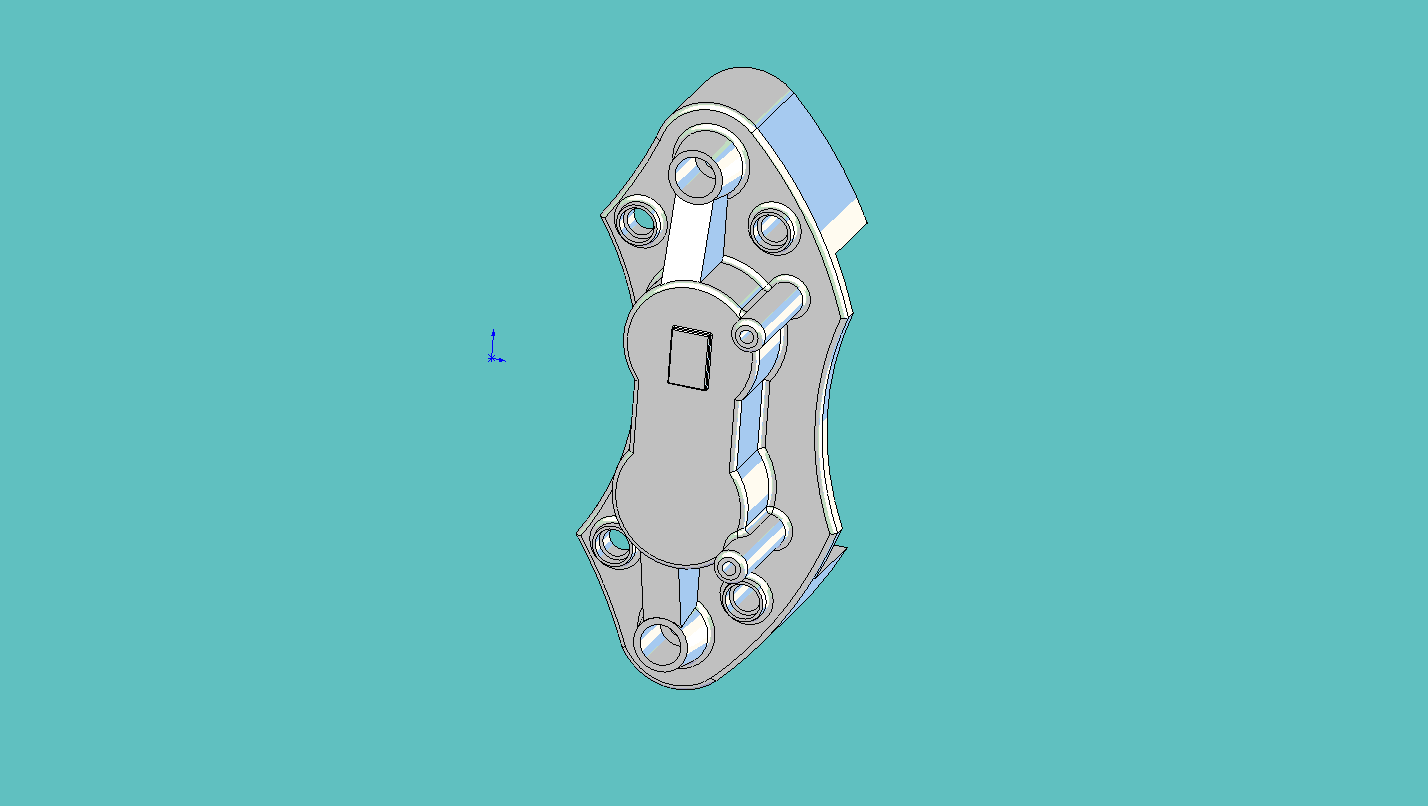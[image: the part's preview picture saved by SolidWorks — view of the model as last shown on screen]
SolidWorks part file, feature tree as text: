
SOLIDWORKS PART (.sldprt)
format: sldprt  version: not decoded by parser v0  size: 2,216,448 bytes
history: native  units: mm
features: sketch x25, cut_extrude x14, fillet x9, extrude x7, mirror x4, plane x3, material x1, chamfer x1, delete_body x1 (+14 scaffold rows collapsed)
feature tree (79):
  scaffold x14  (default folders/planes/origin — collapsed)
  material  "Material <not specified>"
  sketch  "Sketch1"  dims[D1=63.5mm]
  extrude  "Extrude1"  Depth=31.75mm
  sketch  "Sketch5"  dims[D1=~43.962388mm]
  extrude  "Extrude2"  Depth=50.8mm
  sketch  "Sketch3"  dims[D1=50.0mm]
  cut_extrude  "Cut-Extrude1"  Depth=25.4mm
  sketch  "Sketch7"  dims[c1.D1=12.7mm c1.D2=12.7mm c2.D1=~13.906952mm c2.D2=25.0mm c2.D3=25.0mm c3.D1=~12.799272mm c3.D3=152.4mm]
  fillet  "Fillet1"  Radius=2.54mm
  fillet  "Fillet2"  Radius=2.54mm
  fillet  "Fillet3"  Radius=2.54mm
  sketch  "Sketch10"
  cut_extrude  "Cut-Extrude3"  [1 undecoded]
  plane  "Plane1"  Offset=10.16mm
  plane  "Plane2"  Offset=8.636mm
  sketch  "Sketch13"  dims[D1=273.05mm D2=137.16mm]
  cut_extrude  "Cut-Extrude4"  [1 undecoded]
  sketch  "Sketch14"
  cut_extrude  "Cut-Extrude5"  [1 undecoded]
  sketch  "Sketch15"
  extrude  "Extrude3"  Depth=53.18mm
  fillet  "Fillet4"  Radius=2.54mm
  sketch  "Sketch16"  dims[D1=~1.636236mm]
  cut_extrude  "Cut-Extrude6"  Depth=27.94mm
  fillet  "Fillet5"  Radius=2.54mm
  sketch  "Sketch17"
  extrude  "Extrude4"  Depth=2.54mm
  fillet  "Fillet6"  Radius=0.508mm
  chamfer  "Chamfer1"  Distance=1.27mm Angle=45deg
  sketch  "Sketch20"  dims[c1.D1=31.75mm c1.D2=25.4mm c2.D1=~20.003376mm]
  extrude  "Extrude5"  Depth=20.32mm
  cut_extrude  "Cut-Extrude8"  [1 undecoded]
  sketch  "Sketch21"  dims[D1=~4.108238mm]
  cut_extrude  "Cut-Extrude10"  Depth=25.4mm
  fillet  "Fillet7"  Radius=2.54mm
  sketch  "Sketch22"  dims[D1=10.16mm]
  cut_extrude  "Cut-Extrude11"  [1 undecoded]
  sketch  "Sketch24"
  cut_extrude  "Cut-Extrude12"  Depth=22.86mm
  sketch  "Sketch25"  dims[D1=20.574mm]
  extrude  "Extrude6"  Depth=5.08mm
  fillet  "Fillet8"  Radius=2.54mm
  sketch  "Sketch27"  dims[D1=~16.253517mm]
  cut_extrude  "Cut-Extrude15"  Depth=5.08mm
  mirror  "Mirror1"
  sketch  "Sketch29"  dims[D1=7.62mm]
  extrude  "Extrude7"  [1 undecoded]
  sketch  "Sketch30"
  sketch  "Sketch31"  dims[D1=5.08mm]
  cut_extrude  "Cut-Extrude18"  Depth=16.392582mm
  sketch  "Sketch32"  dims[D1=8.89mm]
  cut_extrude  "Cut-Extrude19"  Depth=16.392582mm
  cut_extrude  "Cut-Extrude20"  Depth=43.688mm
  sketch  "Sketch33"
  cut_extrude  "Cut-Extrude21"  Depth=59.69mm
  fillet  "Fillet11"  Radius=2.54mm
  plane  "Plane3"  Offset=94.488mm
  sketch  "Sketch34"  dims[D1=17.62mm]
  sketch  "Sketch36"
  mirror  "Rib3"
  sketch  "Sketch38"
  mirror  "Rib4"
  sketch  "Sketch40"
  mirror  "Rib5"
  delete_body  "Body-Delete1"
decode coverage: 40 of 61 modeling features carry decoded parameters
note: ~ marks probable driven/reference dimensions
note: 6 parameter values undecoded
summary: no parameter record found for 6 features
note: suppression state not decoded; provenance and decode notes live in map.json
